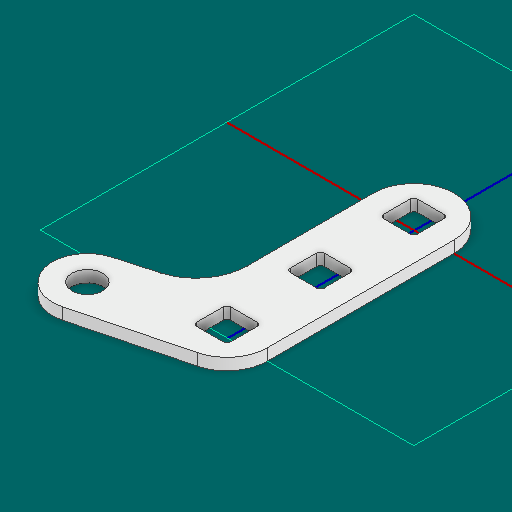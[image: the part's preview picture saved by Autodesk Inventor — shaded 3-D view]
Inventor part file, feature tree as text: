
AUTODESK INVENTOR PART (.ipt)
format: ipt  version: 2025 (Build 290162000, 162)  size: 143,360 bytes
history: native  units: in
note: dims shown in document units (in); Inventor stores cm internally (conversion verified against a paired STEP export)
features: hole x4, other x3, extrude x1, sketch x1
ambient origin geometry x8: Origin, YZ Plane, XZ Plane, XY Plane, X Axis, Y Axis, Z Axis, Center Point
bodies: Solid1 (feature_tree)
feature tree (9):
  other  "Blocks"
  extrude  "Extrusion1"  Depth=0.5in
  sketch  "Sketch1"  dims[d6=0.182in d7=0.182in d8=0.02in d9=0.5in d10=0.5in d12=0.675in d13=0.0625in d14=0.0in]
  other  "main"
  hole  "hole"  [1 undecoded]
  other  "main:1"
  hole  "hole:1"  [1 undecoded]
  hole  "hole:2"  [1 undecoded]
  hole  "hole:3"  [1 undecoded]
note: 4 required parameter values undecoded (feature->parameter linkage not recoverable at this tier; creation-order binding heuristic only, values carry confidence <= 0.55)
